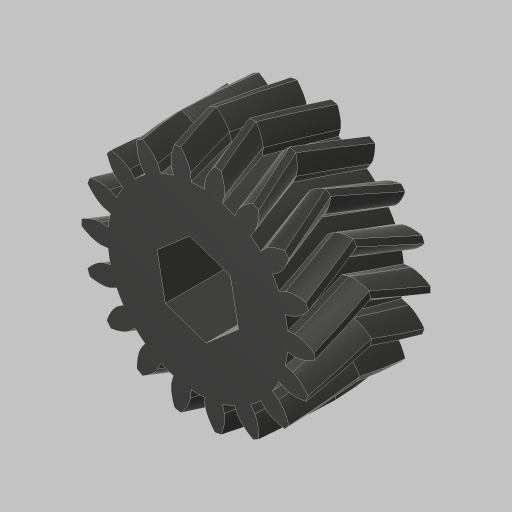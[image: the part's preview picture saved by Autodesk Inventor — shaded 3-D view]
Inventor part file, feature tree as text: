
AUTODESK INVENTOR PART (.ipt)
format: ipt  version: 2023.5 (Build 275446000, 446)  size: 654,848 bytes
history: native  units: in
note: dims shown in document units (in); Inventor stores cm internally (conversion verified against a paired STEP export)
features: other x2, extrude x1, sketch x1
ambient origin geometry x8: Origin, YZ Plane, XZ Plane, XY Plane, X Axis, Y Axis, Z Axis, Center Point
bodies: Solid1 (feature_tree)
feature tree (4):
  extrude  "Extrusion1"  TaperAngle=0.0deg  [1 undecoded]
  other  "DIAMETRIC PITCH"
  sketch  "Sketch1"  dims[d0=0.505in d1=0.0in d2=0.0in d3=1.4173in]
  other  "Helical 2M 18T"
note: 1 required parameter value undecoded (feature->parameter linkage not recoverable at this tier; creation-order binding heuristic only, values carry confidence <= 0.55)
